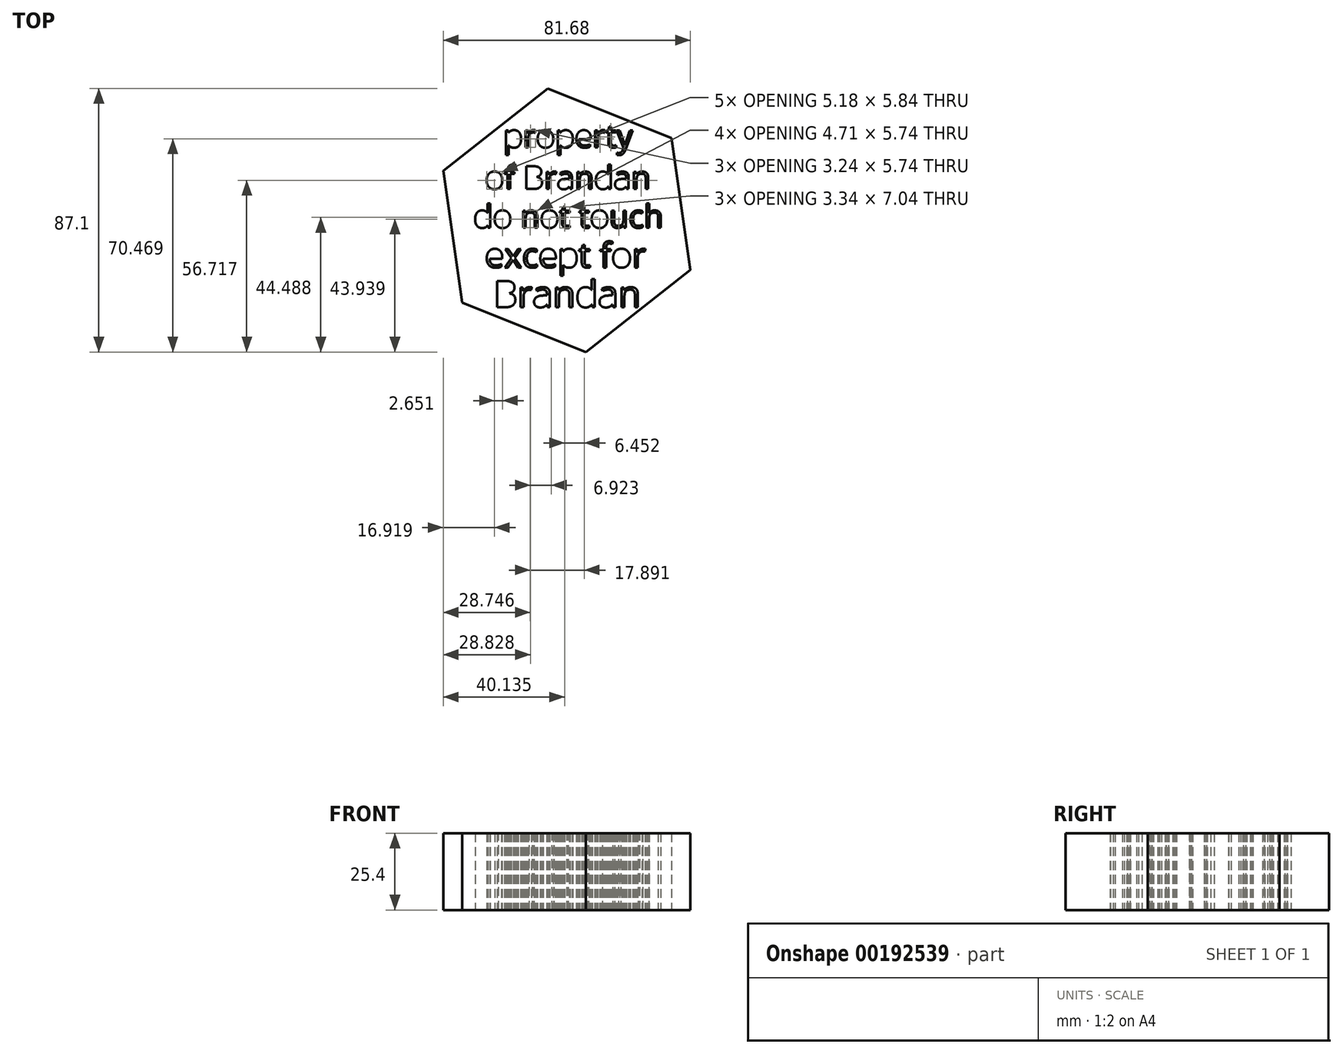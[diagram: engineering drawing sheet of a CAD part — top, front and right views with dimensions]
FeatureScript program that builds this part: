
annotation { "Feature Type Name" : "Feature", "Feature Type Description" : "" }
export const myFeature = defineFeature(function(context is Context, id is Id, definition is map)
    precondition{}
    {
        {
            var Q0;
            Q0=qCreatedBy(makeId("Top.planeOp"),FACE);
            var sketch = newSketch(context, id + "F0", { "sketchPlane" : qUnion([Q0])});
            skCircle(sketch, "E0.cCircle", {"center": v(0, 0) * mm, "radius": 38.1 * mm, "construction": true});
            skLineSegment(sketch, "E0.0", {"start": v(-6.25, 43.55) * mm, "end": v(34.59, 27.19) * mm});
            skLineSegment(sketch, "E0.1", {"start": v(34.59, 27.19) * mm, "end": v(40.84, -16.36) * mm});
            skLineSegment(sketch, "E0.2", {"start": v(40.84, -16.36) * mm, "end": v(6.25, -43.55) * mm});
            skLineSegment(sketch, "E0.3", {"start": v(6.25, -43.55) * mm, "end": v(-34.59, -27.19) * mm});
            skLineSegment(sketch, "E0.4", {"start": v(-34.59, -27.19) * mm, "end": v(-40.84, 16.36) * mm});
            skLineSegment(sketch, "E0.5", {"start": v(-40.84, 16.36) * mm, "end": v(-6.25, 43.55) * mm});
            skPoint(sketch, "E0.0.midPoint", {"position": v(14.17, 35.37) * mm});
            skPoint(sketch, "E1.firstSnap0", {"position": v(-23.54, 29.95) * mm});
            skText(sketch, "E2", { "text": "property", "fontName": "OpenSans-Regular.ttf"});
            skText(sketch, "E3", { "text": "of Brandan", "fontName": "OpenSans-Regular.ttf"});
            skText(sketch, "E4", { "text": "except for", "fontName": "OpenSans-Regular.ttf"});
            skText(sketch, "E5", { "text": "Brandan", "fontName": "OpenSans-Regular.ttf"});
            skText(sketch, "E6", { "text": "do not touch", "fontName": "OpenSans-Regular.ttf"});
            const initialGuessF0  = {"E2": [-0.02099, 0.02405, 1, 0, 0.00758], "E3": [-0.0271, 0.01035, 1, 0, 0.00758], "E4": [-0.0271, -0.0156, 1, 0, 0.00816], "E5": [-0.0242, -0.02871, 1, 0, 0.00874], "E6": [-0.0309, -0.00248, 1, 0, 0.00758]};
            skSetInitialGuess(sketch, initialGuessF0);
            skSolve(sketch);
        }
        {
            var Q0;
            Q0 = qSketchRegion(id + "F0", true);
            extrude(context, id + "F1", {"entities" : qUnion([Q0]), "depth" : 25.4 * mm});
        }
    });
